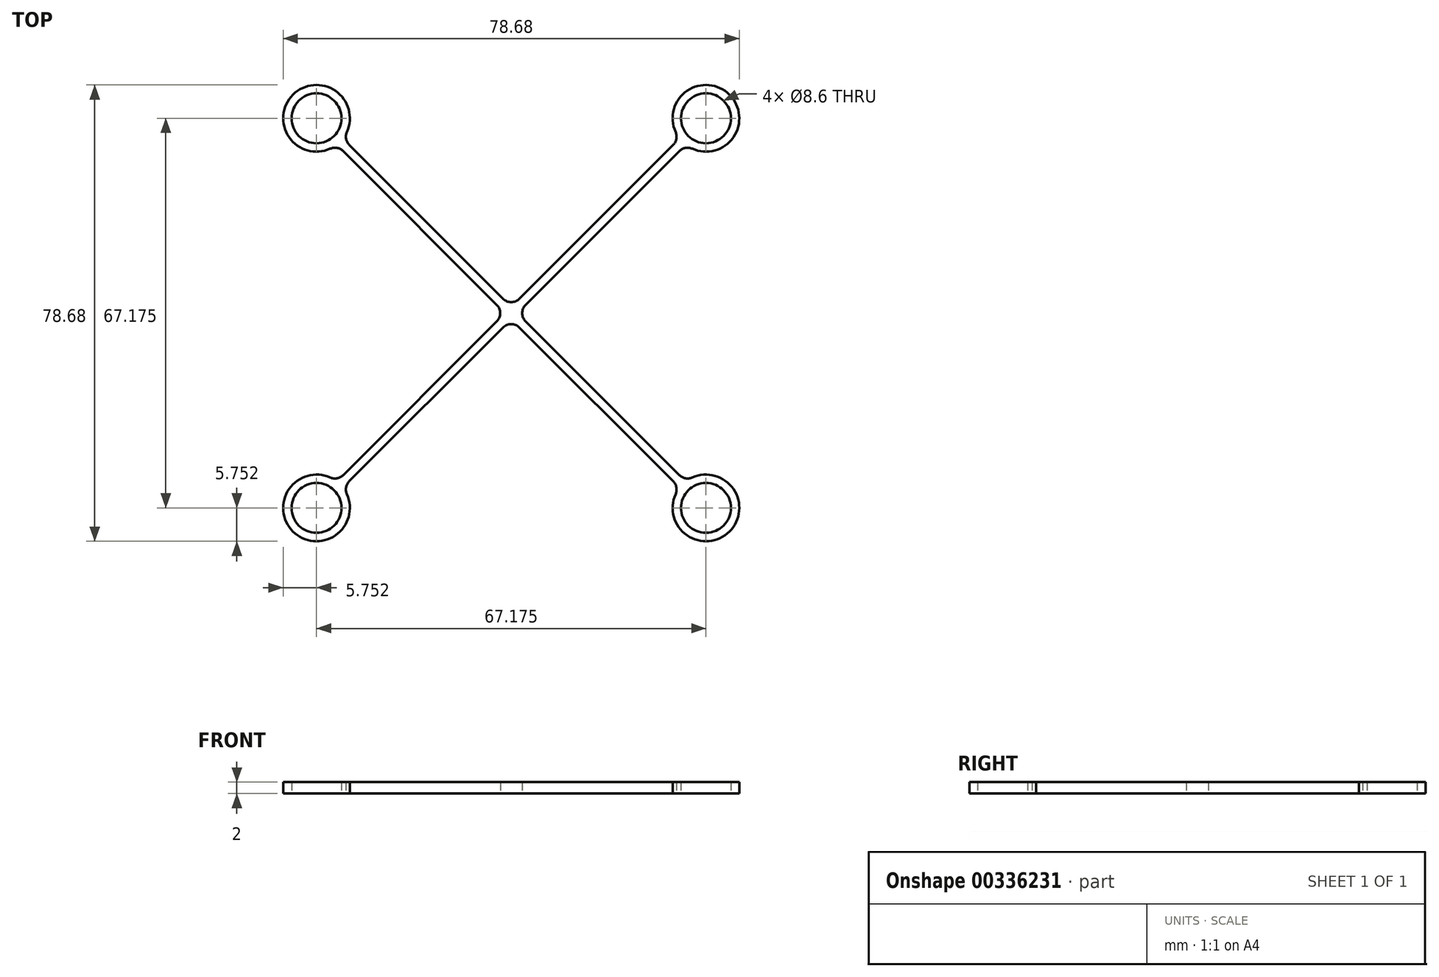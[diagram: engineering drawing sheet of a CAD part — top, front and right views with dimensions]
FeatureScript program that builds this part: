
annotation { "Feature Type Name" : "Feature", "Feature Type Description" : "" }
export const myFeature = defineFeature(function(context is Context, id is Id, definition is map)
    precondition{}
    {
        {
            var Q0;
            Q0=qCreatedBy(makeId("Top.planeOp"),FACE);
            var sketch = newSketch(context, id + "F0", { "sketchPlane" : qUnion([Q0])});
            skLineSegment(sketch, "E0.bottom", {"start": v(33.59, 33.59) * mm, "end": v(-33.59, 33.59) * mm, "construction": true});
            skLineSegment(sketch, "E0.top", {"start": v(33.59, -33.59) * mm, "end": v(-33.59, -33.59) * mm, "construction": true});
            skLineSegment(sketch, "E0.left", {"start": v(33.59, 33.59) * mm, "end": v(33.59, -33.59) * mm, "construction": true});
            skLineSegment(sketch, "E0.right", {"start": v(-33.59, 33.59) * mm, "end": v(-33.59, -33.59) * mm, "construction": true});
            skPoint(sketch, "E0.middle", {"position": v(0, 0) * mm});
            skCircle(sketch, "E1", {"center": v(33.59, 33.59) * mm, "radius": 4.25 * mm, "construction": true});
            skCircle(sketch, "E2", {"center": v(-33.59, 33.59) * mm, "radius": 4.25 * mm, "construction": true});
            skCircle(sketch, "E3", {"center": v(-33.59, -33.59) * mm, "radius": 4.25 * mm, "construction": true});
            skCircle(sketch, "E4", {"center": v(33.59, -33.59) * mm, "radius": 4.25 * mm, "construction": true});
            skLineSegment(sketch, "E5.bottom", {"start": v(10, 16.5) * mm, "end": v(-10, 16.5) * mm, "construction": true});
            skLineSegment(sketch, "E5.top", {"start": v(10, -16.5) * mm, "end": v(-10, -16.5) * mm, "construction": true});
            skLineSegment(sketch, "E5.left", {"start": v(10, 16.5) * mm, "end": v(10, -16.5) * mm, "construction": true});
            skLineSegment(sketch, "E5.right", {"start": v(-10, 16.5) * mm, "end": v(-10, -16.5) * mm, "construction": true});
            skLineSegment(sketch, "E6", {"start": v(33.59, 33.59) * mm, "end": v(-33.59, -33.59) * mm, "construction": true});
            skCircle(sketch, "E7", {"center": v(33.59, 33.59) * mm, "radius": 27.5 * mm, "construction": true});
            skCircle(sketch, "E8", {"center": v(-33.59, 33.59) * mm, "radius": 27.5 * mm, "construction": true});
            skCircle(sketch, "E9", {"center": v(33.59, -33.59) * mm, "radius": 27.5 * mm, "construction": true});
            skCircle(sketch, "E10", {"center": v(-33.59, -33.59) * mm, "radius": 27.5 * mm, "construction": true});
            skSolve(sketch);
        }
        {
            var Q0;
            Q0=qCreatedBy(makeId("Top.planeOp"),FACE);
            var sketch = newSketch(context, id + "F1", { "sketchPlane" : qUnion([Q0])});
            skCircle(sketch, "E11.0", {"center": v(33.59, 33.59) * mm, "radius": 4.3 * mm});
            skLineSegment(sketch, "E12", {"start": v(33.59, 33.59) * mm, "end": v(0, 0) * mm, "construction": true});
            skArc(sketch, "E13.0", {"start": v(30.09, 29.03) * mm, "mid": v(37.65, 37.65) * mm, "end": v(29.03, 30.09) * mm});
            skLineSegment(sketch, "E14", {"start": v(29.03, 30.09) * mm, "end": v(0, 1.06) * mm});
            skLineSegment(sketch, "E15", {"start": v(30.09, 29.03) * mm, "end": v(1.06, 0) * mm});
            skCircle(sketch, "E16.1.0", {"center": v(-33.59, 33.59) * mm, "radius": 4.3 * mm});
            skArc(sketch, "E16.1.1", {"start": v(-29.03, 30.09) * mm, "mid": v(-37.65, 37.65) * mm, "end": v(-30.09, 29.03) * mm});
            skLineSegment(sketch, "E16.1.2", {"start": v(-29.03, 30.09) * mm, "end": v(0, 1.06) * mm});
            skLineSegment(sketch, "E16.1.3", {"start": v(-30.09, 29.03) * mm, "end": v(-1.06, 0) * mm});
            skCircle(sketch, "E16.2.0", {"center": v(-33.59, -33.59) * mm, "radius": 4.3 * mm});
            skArc(sketch, "E16.2.1", {"start": v(-30.09, -29.03) * mm, "mid": v(-37.65, -37.65) * mm, "end": v(-29.03, -30.09) * mm});
            skLineSegment(sketch, "E16.2.2", {"start": v(-30.09, -29.03) * mm, "end": v(-1.06, 0) * mm});
            skLineSegment(sketch, "E16.2.3", {"start": v(-29.03, -30.09) * mm, "end": v(0, -1.06) * mm});
            skCircle(sketch, "E16.3.0", {"center": v(33.59, -33.59) * mm, "radius": 4.3 * mm});
            skArc(sketch, "E16.3.1", {"start": v(29.03, -30.09) * mm, "mid": v(37.65, -37.65) * mm, "end": v(30.09, -29.03) * mm});
            skLineSegment(sketch, "E16.3.2", {"start": v(29.03, -30.09) * mm, "end": v(0, -1.06) * mm});
            skLineSegment(sketch, "E16.3.3", {"start": v(30.09, -29.03) * mm, "end": v(1.06, 0) * mm});
            skPoint(sketch, "E16.center", {"position": v(0, 0) * mm});
            skSolve(sketch);
        }
        {
            var Q0;
            Q0 = qSketchRegion(id + "F1", true);
            extrude(context, id + "F2", {"entities" : qUnion([Q0]), "depth" : 2 * mm});
        }
        {
            var Q0;
            Q0=makeQuery(id+"F2.opExtrude","SWEPT_EDGE",EDGE,{"disambiguationData":[OSD([sQuery(id+"F1.wireOp",EDGE,"E13.0"),sQuery(id+"F1.wireOp",EDGE,"E15")])]});
            var Q1;
            Q1=makeQuery(id+"F2.opExtrude","SWEPT_EDGE",EDGE,{"disambiguationData":[OSD([sQuery(id+"F1.wireOp",EDGE,"E13.0"),sQuery(id+"F1.wireOp",EDGE,"E14")])]});
            var Q2;
            Q2=makeQuery(id+"F2.opExtrude","SWEPT_EDGE",EDGE,{"disambiguationData":[OSD([sQuery(id+"F1.wireOp",EDGE,"E15"),sQuery(id+"F1.wireOp",EDGE,"E16.3.3")])]});
            var Q3;
            Q3=makeQuery(id+"F2.opExtrude","SWEPT_EDGE",EDGE,{"disambiguationData":[OSD([sQuery(id+"F1.wireOp",EDGE,"E16.2.3"),sQuery(id+"F1.wireOp",EDGE,"E16.3.2")])]});
            var Q4;
            Q4=makeQuery(id+"F2.opExtrude","SWEPT_EDGE",EDGE,{"disambiguationData":[OSD([sQuery(id+"F1.wireOp",EDGE,"E16.1.3"),sQuery(id+"F1.wireOp",EDGE,"E16.2.2")])]});
            var Q5;
            Q5=makeQuery(id+"F2.opExtrude","SWEPT_EDGE",EDGE,{"disambiguationData":[OSD([sQuery(id+"F1.wireOp",EDGE,"E14"),sQuery(id+"F1.wireOp",EDGE,"E16.1.2")])]});
            var Q6;
            Q6=makeQuery(id+"F2.opExtrude","SWEPT_EDGE",EDGE,{"disambiguationData":[OSD([sQuery(id+"F1.wireOp",EDGE,"E16.3.1"),sQuery(id+"F1.wireOp",EDGE,"E16.3.2")])]});
            var Q7;
            Q7=makeQuery(id+"F2.opExtrude","SWEPT_EDGE",EDGE,{"disambiguationData":[OSD([sQuery(id+"F1.wireOp",EDGE,"E16.3.1"),sQuery(id+"F1.wireOp",EDGE,"E16.3.3")])]});
            var Q8;
            Q8=makeQuery(id+"F2.opExtrude","SWEPT_EDGE",EDGE,{"disambiguationData":[OSD([sQuery(id+"F1.wireOp",EDGE,"E16.1.1"),sQuery(id+"F1.wireOp",EDGE,"E16.1.3")])]});
            var Q9;
            Q9=makeQuery(id+"F2.opExtrude","SWEPT_EDGE",EDGE,{"disambiguationData":[OSD([sQuery(id+"F1.wireOp",EDGE,"E16.2.1"),sQuery(id+"F1.wireOp",EDGE,"E16.2.3")])]});
            var Q10;
            Q10=makeQuery(id+"F2.opExtrude","SWEPT_EDGE",EDGE,{"disambiguationData":[OSD([sQuery(id+"F1.wireOp",EDGE,"E16.1.1"),sQuery(id+"F1.wireOp",EDGE,"E16.1.2")])]});
            var Q11;
            Q11=makeQuery(id+"F2.opExtrude","SWEPT_EDGE",EDGE,{"disambiguationData":[OSD([sQuery(id+"F1.wireOp",EDGE,"E16.2.1"),sQuery(id+"F1.wireOp",EDGE,"E16.2.2")])]});
            fillet(context, id + "F3", {"entities" : qUnion([Q0, Q1, Q2, Q3, Q4, Q5, Q6, Q7, Q8, Q9, Q10, Q11]), "radius" : 2 * mm, "allowEdgeOverflow" : false});
        }
    });
